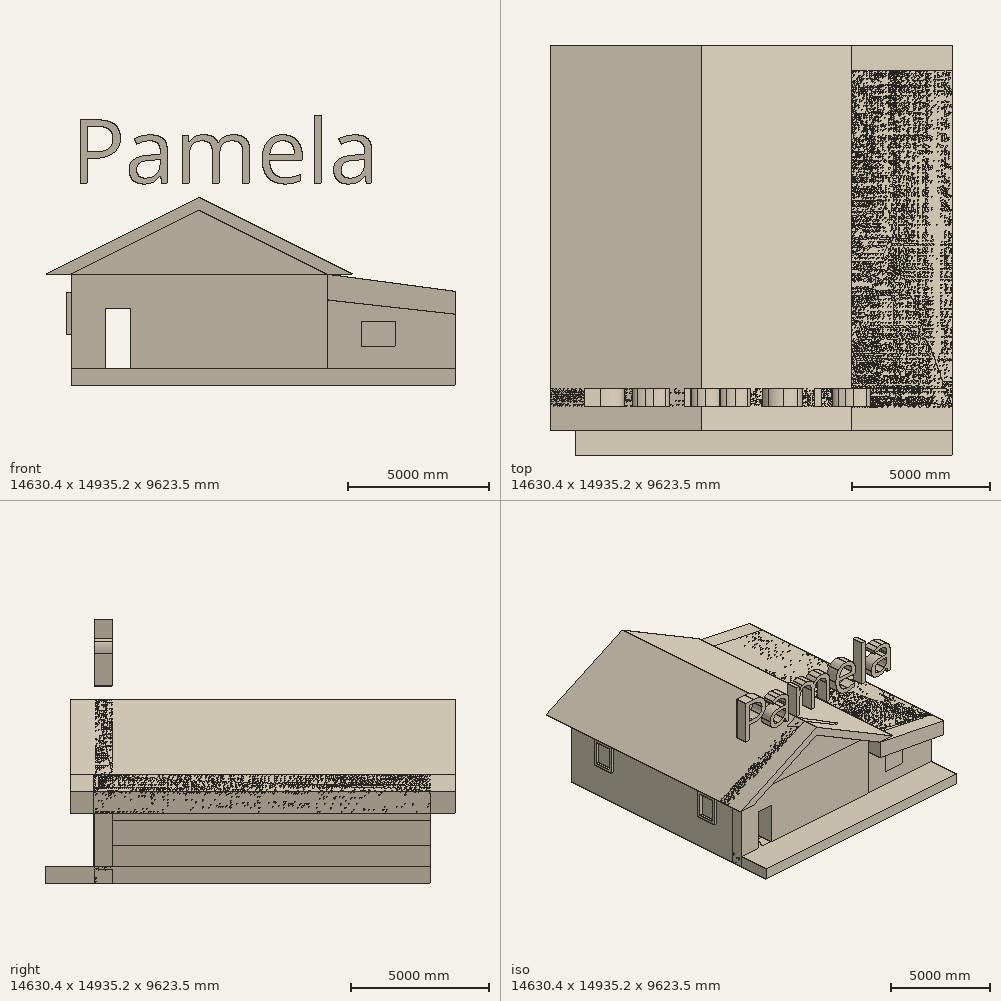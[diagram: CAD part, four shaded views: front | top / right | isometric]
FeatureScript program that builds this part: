
annotation { "Feature Type Name" : "Feature", "Feature Type Description" : "" }
export const myFeature = defineFeature(function(context is Context, id is Id, definition is map)
    precondition{}
    {
        {
            var Q0;
            Q0=qCreatedBy(makeId("Front.planeOp"),FACE);
            var sketch = newSketch(context, id + "F0", { "sketchPlane" : qUnion([Q0])});
            skLineSegment(sketch, "E0", {"start": v(0, 0) * mm, "end": v(-4572, 0) * mm});
            skLineSegment(sketch, "E1", {"start": v(0, 0) * mm, "end": v(4572, 0) * mm});
            skLineSegment(sketch, "E2", {"start": v(0, 0) * mm, "end": v(0, 2286) * mm});
            skLineSegment(sketch, "E3", {"start": v(0, 2286) * mm, "end": v(-4572, 0) * mm});
            skLineSegment(sketch, "E4", {"start": v(0, 2286) * mm, "end": v(4572, 0) * mm});
            skLineSegment(sketch, "E5", {"start": v(-4572, 0) * mm, "end": v(-5486.4, 0) * mm});
            skLineSegment(sketch, "E6", {"start": v(4572, 0) * mm, "end": v(5486.4, 0) * mm});
            skLineSegment(sketch, "E7", {"start": v(0, 2286) * mm, "end": v(0, 2743.2) * mm});
            skLineSegment(sketch, "E8", {"start": v(0, 2743.2) * mm, "end": v(-5486.4, 0) * mm});
            skLineSegment(sketch, "E9", {"start": v(0, 2743.2) * mm, "end": v(5486.4, 0) * mm});
            skLineSegment(sketch, "E10", {"start": v(-4572, 0) * mm, "end": v(-4572, -3352.8) * mm});
            skLineSegment(sketch, "E11", {"start": v(4572, 0) * mm, "end": v(4572, -3352.8) * mm});
            skLineSegment(sketch, "E12", {"start": v(-4572, -3352.8) * mm, "end": v(4572, -3352.8) * mm});
            skLineSegment(sketch, "E13", {"start": v(-4572, -3352.8) * mm, "end": v(-4572, -3962.4) * mm});
            skLineSegment(sketch, "E14", {"start": v(4572, -3352.8) * mm, "end": v(4572, -3962.4) * mm});
            skLineSegment(sketch, "E15", {"start": v(-4572, -3962.4) * mm, "end": v(4572, -3962.4) * mm});
            skLineSegment(sketch, "E16.bottom", {"start": v(-3352.8, -3352.8) * mm, "end": v(-2438.4, -3352.8) * mm});
            skLineSegment(sketch, "E16.top", {"start": v(-3352.8, -1219.2) * mm, "end": v(-2438.4, -1219.2) * mm});
            skLineSegment(sketch, "E16.left", {"start": v(-3352.8, -3352.8) * mm, "end": v(-3352.8, -1219.2) * mm});
            skLineSegment(sketch, "E16.right", {"start": v(-2438.4, -3352.8) * mm, "end": v(-2438.4, -1219.2) * mm});
            skLineSegment(sketch, "E17.0", {"start": v(-2133.6, -3352.8) * mm, "end": v(-2133.6, -914.4) * mm});
            skLineSegment(sketch, "E17.1", {"start": v(-3657.6, -914.4) * mm, "end": v(-2133.6, -914.4) * mm});
            skLineSegment(sketch, "E17.2", {"start": v(-3657.6, -3352.8) * mm, "end": v(-3657.6, -914.4) * mm});
            skLineSegment(sketch, "E18.bottom", {"start": v(-609.6, -1219.2) * mm, "end": v(3962.4, -1219.2) * mm});
            skLineSegment(sketch, "E18.top", {"start": v(-609.6, -2590.8) * mm, "end": v(3962.4, -2590.8) * mm});
            skLineSegment(sketch, "E18.left", {"start": v(-609.6, -1219.2) * mm, "end": v(-609.6, -2590.8) * mm});
            skLineSegment(sketch, "E18.right", {"start": v(3962.4, -1219.2) * mm, "end": v(3962.4, -2590.8) * mm});
            skLineSegment(sketch, "E19.0", {"start": v(-457.2, -1371.6) * mm, "end": v(-457.2, -2438.4) * mm});
            skLineSegment(sketch, "E19.1", {"start": v(-457.2, -1371.6) * mm, "end": v(3810, -1371.6) * mm});
            skLineSegment(sketch, "E19.2", {"start": v(3810, -1371.6) * mm, "end": v(3810, -2438.4) * mm});
            skLineSegment(sketch, "E19.3", {"start": v(-457.2, -2438.4) * mm, "end": v(3810, -2438.4) * mm});
            skLineSegment(sketch, "E20", {"start": v(4572, -3352.8) * mm, "end": v(9144, -3352.8) * mm});
            skLineSegment(sketch, "E21", {"start": v(9144, -3352.8) * mm, "end": v(9144, -609.6) * mm});
            skLineSegment(sketch, "E22", {"start": v(9144, -609.6) * mm, "end": v(4572, 0) * mm});
            skLineSegment(sketch, "E23", {"start": v(4572, 0) * mm, "end": v(4572, -914.4) * mm});
            skLineSegment(sketch, "E24", {"start": v(4572, -914.4) * mm, "end": v(9144, -1426.46) * mm});
            skLineSegment(sketch, "E25.bottom", {"start": v(4572, -3962.4) * mm, "end": v(9144, -3962.4) * mm});
            skLineSegment(sketch, "E25.left", {"start": v(4572, -3962.4) * mm, "end": v(4572, -3352.8) * mm});
            skLineSegment(sketch, "E25.right", {"start": v(9144, -3962.4) * mm, "end": v(9144, -3352.8) * mm});
            skLineSegment(sketch, "E26.bottom", {"start": v(5791.2, -1676.4) * mm, "end": v(7010.4, -1676.4) * mm});
            skLineSegment(sketch, "E26.top", {"start": v(5791.2, -2590.8) * mm, "end": v(7010.4, -2590.8) * mm});
            skLineSegment(sketch, "E26.left", {"start": v(5791.2, -1676.4) * mm, "end": v(5791.2, -2590.8) * mm});
            skLineSegment(sketch, "E26.right", {"start": v(7010.4, -1676.4) * mm, "end": v(7010.4, -2590.8) * mm});
            skLineSegment(sketch, "E27.0", {"start": v(5943.6, -1828.8) * mm, "end": v(6858, -1828.8) * mm});
            skLineSegment(sketch, "E27.1", {"start": v(5943.6, -1828.8) * mm, "end": v(5943.6, -2438.4) * mm});
            skLineSegment(sketch, "E27.2", {"start": v(5943.6, -2438.4) * mm, "end": v(6858, -2438.4) * mm});
            skLineSegment(sketch, "E27.3", {"start": v(6858, -1828.8) * mm, "end": v(6858, -2438.4) * mm});
            skText(sketch, "E28", { "text": "Pamela", "fontName": "OpenSans-Regular.ttf"});
            const initialGuessF0  = {"E28": [-4.55727, 3.25068, 1, 0, 2.28398]};
            skSetInitialGuess(sketch, initialGuessF0);
            skSolve(sketch);
        }
        {
            var Q0;
            Q0=makeQuery(id+"F0.imprint","IMPRINT",FACE,{"disambiguationData":[TD([[makeQuery(id+"F0.imprint","IMPRINT",EDGE,{"derivedFrom":sQuery(id+"F0.wireOp",EDGE,"E3")}),-1.0]])]});
            var Q1;
            Q1=makeQuery(id+"F0.imprint","IMPRINT",FACE,{"disambiguationData":[TD([[makeQuery(id+"F0.imprint","IMPRINT",EDGE,{"derivedFrom":sQuery(id+"F0.wireOp",EDGE,"E4")}),1.0]])]});
            extrude(context, id + "F1", {"entities" : qUnion([Q0, Q1]), "depth" : 914.4 * mm, "offsetDistance" : 30.48 * mm, "hasSecondDirection" : true, "secondDirectionOppositeDirection" : true, "secondDirectionDepth" : 13106.4 * mm});
        }
        {
            var Q0;
            Q0=makeQuery(id+"F0.imprint","IMPRINT",FACE,{"disambiguationData":[TD([[makeQuery(id+"F0.imprint","IMPRINT",EDGE,{"derivedFrom":sQuery(id+"F0.wireOp",EDGE,"E0")}),-1.0]])]});
            var Q1;
            Q1=makeQuery(id+"F0.imprint","IMPRINT",FACE,{"disambiguationData":[TD([[makeQuery(id+"F0.imprint","IMPRINT",EDGE,{"derivedFrom":sQuery(id+"F0.wireOp",EDGE,"E1")}),1.0]])]});
            extrude(context, id + "F2", {"entities" : qUnion([Q0, Q1]), "operationType" : NewBodyOperationType.ADD, "depth" : 60.96 * mm, "offsetDistance" : 30.48 * mm, "hasSecondDirection" : true, "secondDirectionOppositeDirection" : true, "secondDirectionDepth" : 12192 * mm});
        }
        {
            var Q0;
            {var subQ0=sQuery(id+"F0.wireOp",EDGE,"E22");Q0=makeQuery(id+"F0.imprint","IMPRINT",FACE,{"disambiguationData":[TD([[makeQuery(id+"F0.imprint","IMPRINT",EDGE,{"derivedFrom":subQ0}),1.0]])]});}
            extrude(context, id + "F3", {"entities" : qUnion([Q0]), "depth" : 914.4 * mm, "offsetDistance" : 30.48 * mm, "hasSecondDirection" : true, "secondDirectionOppositeDirection" : true, "secondDirectionDepth" : 13106.4 * mm});
        }
        {
            var Q0;
            Q0=makeQuery(id+"F0.imprint","IMPRINT",FACE,{"disambiguationData":[TD([[makeQuery(id+"F0.imprint","IMPRINT",EDGE,{"derivedFrom":sQuery(id+"F0.wireOp",EDGE,"E0")}),1.0]])]});
            var Q1;
            Q1=makeQuery(id+"F0.imprint","IMPRINT",FACE,{"disambiguationData":[TD([[makeQuery(id+"F0.imprint","IMPRINT",EDGE,{"derivedFrom":sQuery(id+"F0.wireOp",EDGE,"E19.0")}),1.0]])]});
            var Q2;
            Q2=makeQuery(id+"F0.imprint","IMPRINT",FACE,{"disambiguationData":[TD([[makeQuery(id+"F0.imprint","IMPRINT",EDGE,{"derivedFrom":sQuery(id+"F0.wireOp",EDGE,"E18.bottom")}),-1.0]])]});
            var Q3;
            Q3=makeQuery(id+"F0.imprint","IMPRINT",FACE,{"disambiguationData":[TD([[makeQuery(id+"F0.imprint","IMPRINT",EDGE,{"derivedFrom":sQuery(id+"F0.wireOp",EDGE,"E16.bottom")}),1.0]])]});
            var Q4;
            Q4=makeQuery(id+"F0.imprint","IMPRINT",FACE,{"disambiguationData":[TD([[makeQuery(id+"F0.imprint","IMPRINT",EDGE,{"derivedFrom":sQuery(id+"F0.wireOp",EDGE,"E16.top")}),1.0]])]});
            var Q5;
            Q5=makeQuery(id+"F0.imprint","IMPRINT",FACE,{"disambiguationData":[TD([[makeQuery(id+"F0.imprint","IMPRINT",EDGE,{"derivedFrom":sQuery(id+"F0.wireOp",EDGE,"E27.0")}),-1.0]])]});
            var Q6;
            Q6=makeQuery(id+"F0.imprint","IMPRINT",FACE,{"disambiguationData":[TD([[makeQuery(id+"F0.imprint","IMPRINT",EDGE,{"derivedFrom":sQuery(id+"F0.wireOp",EDGE,"E11")}),1.0]])]});
            var Q7;
            Q7=makeQuery(id+"F0.imprint","IMPRINT",FACE,{"disambiguationData":[TD([[makeQuery(id+"F0.imprint","IMPRINT",EDGE,{"derivedFrom":sQuery(id+"F0.wireOp",EDGE,"E26.bottom")}),-1.0]])]});
            extrude(context, id + "F4", {"entities" : qUnion([Q0, Q1, Q2, Q3, Q4, Q5, Q6, Q7]), "depth" : 60.96 * mm, "offsetDistance" : 30.48 * mm, "hasSecondDirection" : true, "secondDirectionOppositeDirection" : true, "secondDirectionDepth" : 12192 * mm});
        }
        {
            var Q0;
            Q0=sQuery(id+"F0.wireOp",EDGE,"E16.left");
            var Q1;
            Q1=sQuery(id+"F0.wireOp",EDGE,"E16.top");
            var Q2;
            Q2=sQuery(id+"F0.wireOp",EDGE,"E16.right");
            var Q3;
            Q3=sQuery(id+"F0.wireOp",EDGE,"E17.0");
            var Q4;
            Q4=sQuery(id+"F0.wireOp",EDGE,"E17.1");
            var Q5;
            Q5=sQuery(id+"F0.wireOp",EDGE,"E17.2");
            var Q6;
            Q6=sQuery(id+"F0.wireOp",EDGE,"E18.left");
            var Q7;
            Q7=sQuery(id+"F0.wireOp",EDGE,"E19.0");
            var Q8;
            Q8=sQuery(id+"F0.wireOp",EDGE,"E19.3");
            var Q9;
            Q9=sQuery(id+"F0.wireOp",EDGE,"E18.top");
            var Q10;
            Q10=sQuery(id+"F0.wireOp",EDGE,"E18.right");
            var Q11;
            Q11=sQuery(id+"F0.wireOp",EDGE,"E19.2");
            var Q12;
            Q12=sQuery(id+"F0.wireOp",EDGE,"E19.1");
            var Q13;
            Q13=sQuery(id+"F0.wireOp",EDGE,"E18.bottom");
            var Q14;
            Q14=sQuery(id+"F0.wireOp",EDGE,"E26.left");
            var Q15;
            Q15=sQuery(id+"F0.wireOp",EDGE,"E26.top");
            var Q16;
            Q16=sQuery(id+"F0.wireOp",EDGE,"E26.right");
            var Q17;
            Q17=sQuery(id+"F0.wireOp",EDGE,"E26.bottom");
            var Q18;
            Q18=sQuery(id+"F0.wireOp",EDGE,"E27.0");
            var Q19;
            Q19=sQuery(id+"F0.wireOp",EDGE,"E27.3");
            var Q20;
            Q20=sQuery(id+"F0.wireOp",EDGE,"E27.1");
            var Q21;
            Q21=sQuery(id+"F0.wireOp",EDGE,"E27.2");
            extrude(context, id + "F5", {"bodyType" : ToolBodyType.SURFACE, "surfaceEntities" : qUnion([Q0, Q1, Q2, Q3, Q4, Q5, Q6, Q7, Q8, Q9, Q10, Q11, Q12, Q13, Q14, Q15, Q16, Q17, Q18, Q19, Q20, Q21]), "depth" : 243.84 * mm, "offsetDistance" : 30.48 * mm});
        }
        {
            var Q0;
            {var subQ5=sQuery(id+"F0.wireOp",EDGE,"E13");Q0=makeQuery(id+"F0.imprint","IMPRINT",FACE,{"disambiguationData":[TD([[makeQuery(id+"F0.imprint","IMPRINT",EDGE,{"derivedFrom":subQ5}),1.0]])]});}
            var Q1;
            Q1=makeQuery(id+"F0.imprint","IMPRINT",FACE,{"disambiguationData":[TD([[makeQuery(id+"F0.imprint","IMPRINT",EDGE,{"derivedFrom":sQuery(id+"F0.wireOp",EDGE,"E25.bottom")}),1.0]])]});
            extrude(context, id + "F6", {"entities" : qUnion([Q0, Q1]), "operationType" : NewBodyOperationType.ADD, "depth" : 1828.8 * mm, "offsetDistance" : 30.48 * mm, "hasSecondDirection" : true, "secondDirectionOppositeDirection" : true, "secondDirectionDepth" : 12192 * mm});
        }
        {
            var Q0;
            Q0 = qSketchRegion(id + "F0", true);
            extrude(context, id + "F7", {"entities" : qUnion([Q0]), "depth" : 30.48 * mm, "offsetDistance" : 30.48 * mm, "hasSecondDirection" : true, "secondDirectionOppositeDirection" : true, "secondDirectionDepth" : 609.6 * mm});
        }
        {
            var Q0;
            Q0=makeQuery(id+"F6.boolean.opBoolean","MERGE",FACE,{"derivedFrom":[makeQuery(id+"F4.opExtrude","SWEPT_FACE",FACE,{"disambiguationData":[OSD([sQuery(id+"F0.wireOp",EDGE,"E10")])]}),makeQuery(id+"F6.opExtrude","SWEPT_FACE",FACE,{"disambiguationData":[OSD([sQuery(id+"F0.wireOp",EDGE,"E13")])]})]});
            var sketch = newSketch(context, id + "F8", { "sketchPlane" : qUnion([Q0])});
            skLineSegment(sketch, "E29.bottom", {"start": v(-10393.68, -640.08) * mm, "end": v(-9174.48, -640.08) * mm});
            skLineSegment(sketch, "E29.top", {"start": v(-10393.68, -2164.08) * mm, "end": v(-9174.48, -2164.08) * mm});
            skLineSegment(sketch, "E29.left", {"start": v(-10393.68, -640.08) * mm, "end": v(-10393.68, -2164.08) * mm});
            skLineSegment(sketch, "E29.right", {"start": v(-9174.48, -640.08) * mm, "end": v(-9174.48, -2164.08) * mm});
            skLineSegment(sketch, "E30.0", {"start": v(-10241.28, -792.48) * mm, "end": v(-9326.88, -792.48) * mm});
            skLineSegment(sketch, "E30.1", {"start": v(-10241.28, -792.48) * mm, "end": v(-10241.28, -2011.68) * mm});
            skLineSegment(sketch, "E30.2", {"start": v(-10241.28, -2011.68) * mm, "end": v(-9326.88, -2011.68) * mm});
            skLineSegment(sketch, "E30.3", {"start": v(-9326.88, -792.48) * mm, "end": v(-9326.88, -2011.68) * mm});
            skLineSegment(sketch, "E31.bottom", {"start": v(-2956.56, -2164.08) * mm, "end": v(-1737.36, -2164.08) * mm});
            skLineSegment(sketch, "E31.top", {"start": v(-2956.56, -640.08) * mm, "end": v(-1737.36, -640.08) * mm});
            skLineSegment(sketch, "E31.left", {"start": v(-2956.56, -2164.08) * mm, "end": v(-2956.56, -640.08) * mm});
            skLineSegment(sketch, "E31.right", {"start": v(-1737.36, -2164.08) * mm, "end": v(-1737.36, -640.08) * mm});
            skLineSegment(sketch, "E32.0", {"start": v(-2804.16, -792.48) * mm, "end": v(-1889.76, -792.48) * mm});
            skLineSegment(sketch, "E32.1", {"start": v(-2804.16, -2011.68) * mm, "end": v(-2804.16, -792.48) * mm});
            skLineSegment(sketch, "E32.2", {"start": v(-2804.16, -2011.68) * mm, "end": v(-1889.76, -2011.68) * mm});
            skLineSegment(sketch, "E32.3", {"start": v(-1889.76, -2011.68) * mm, "end": v(-1889.76, -792.48) * mm});
            skSolve(sketch);
        }
        {
            var Q0;
            Q0=makeQuery(id+"F8.imprint","IMPRINT",FACE,{"disambiguationData":[TD([[makeQuery(id+"F8.imprint","IMPRINT",EDGE,{"derivedFrom":sQuery(id+"F8.wireOp",EDGE,"E31.bottom")}),1.0]])]});
            var Q1;
            Q1=makeQuery(id+"F8.imprint","IMPRINT",FACE,{"disambiguationData":[TD([[makeQuery(id+"F8.imprint","IMPRINT",EDGE,{"derivedFrom":sQuery(id+"F8.wireOp",EDGE,"E29.bottom")}),-1.0]])]});
            extrude(context, id + "F9", {"entities" : qUnion([Q0, Q1]), "operationType" : NewBodyOperationType.ADD, "depth" : 152.4 * mm, "offsetDistance" : 30.48 * mm});
        }
    });
